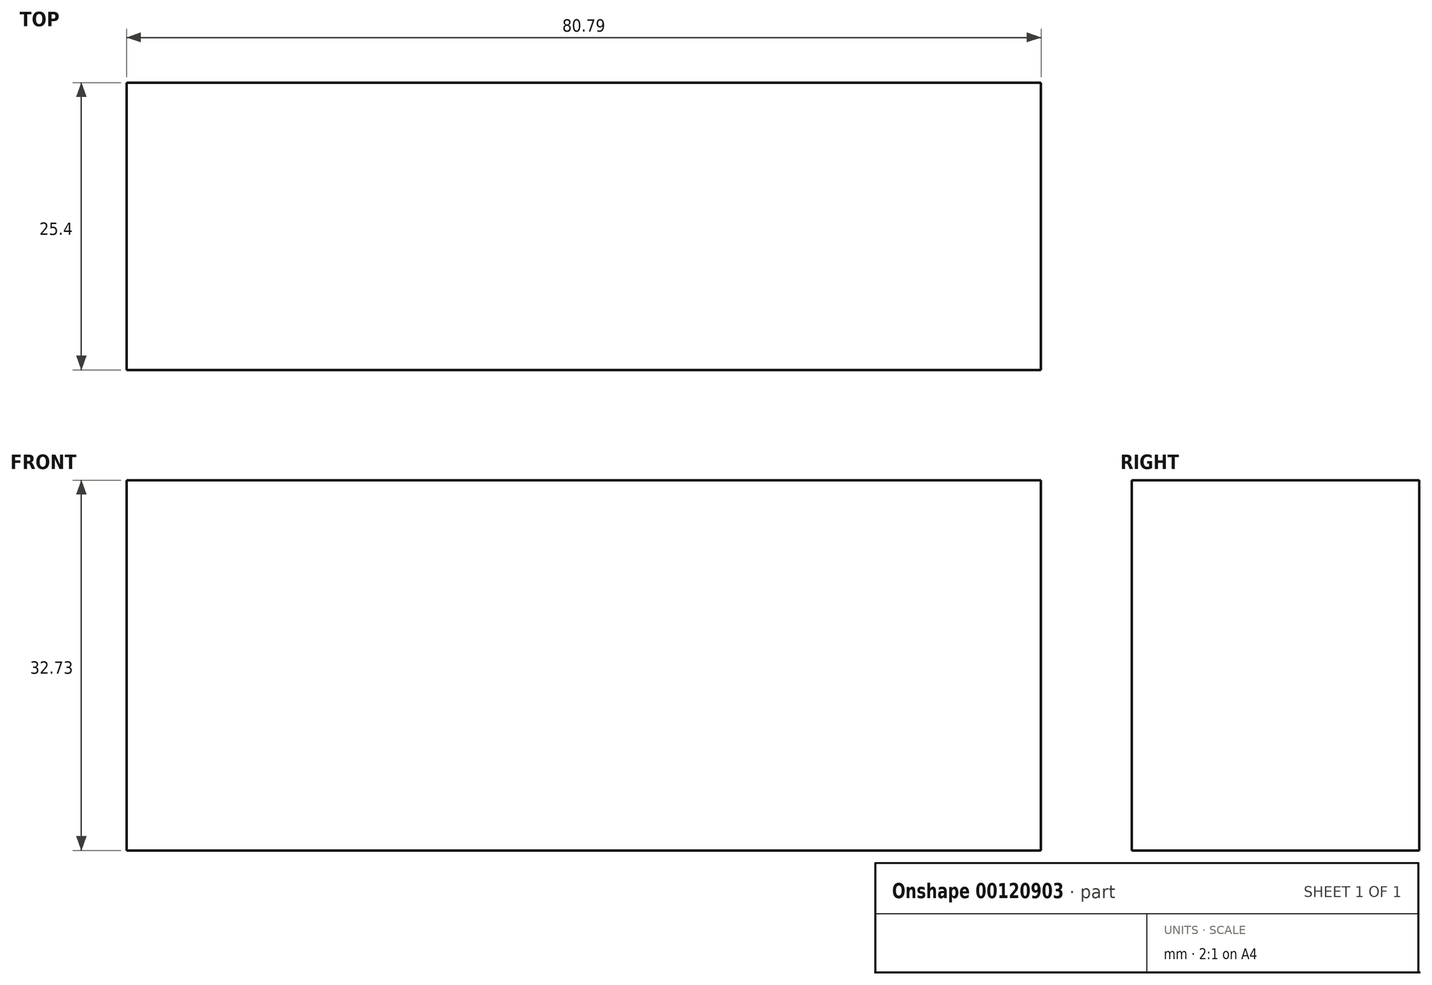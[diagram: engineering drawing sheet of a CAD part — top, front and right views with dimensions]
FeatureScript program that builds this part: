
annotation { "Feature Type Name" : "Feature", "Feature Type Description" : "" }
export const myFeature = defineFeature(function(context is Context, id is Id, definition is map)
    precondition{}
    {
        {
            var Q0;
            Q0=qCreatedBy(makeId("Front.planeOp"),FACE);
            var sketch = newSketch(context, id + "F0", { "sketchPlane" : qUnion([Q0])});
            skLineSegment(sketch, "E0.bottom", {"start": v(-48.47, 53.44) * mm, "end": v(32.32, 53.44) * mm});
            skLineSegment(sketch, "E0.top", {"start": v(-48.47, 20.7) * mm, "end": v(32.32, 20.7) * mm});
            skLineSegment(sketch, "E0.left", {"start": v(-48.47, 53.44) * mm, "end": v(-48.47, 20.7) * mm});
            skLineSegment(sketch, "E0.right", {"start": v(32.32, 53.44) * mm, "end": v(32.32, 20.7) * mm});
            skSolve(sketch);
        }
        {
            var Q0;
            Q0=makeQuery(id+"F0.imprint","IMPRINT",FACE,{"disambiguationData":[TD([[makeQuery(id+"F0.imprint","IMPRINT",EDGE,{"derivedFrom":sQuery(id+"F0.wireOp",EDGE,"E0.bottom")}),-1.0]])]});
            extrude(context, id + "F1", {"entities" : qUnion([Q0]), "depth" : 25.4 * mm, "offsetDistance" : 25.4 * mm});
        }
    });
